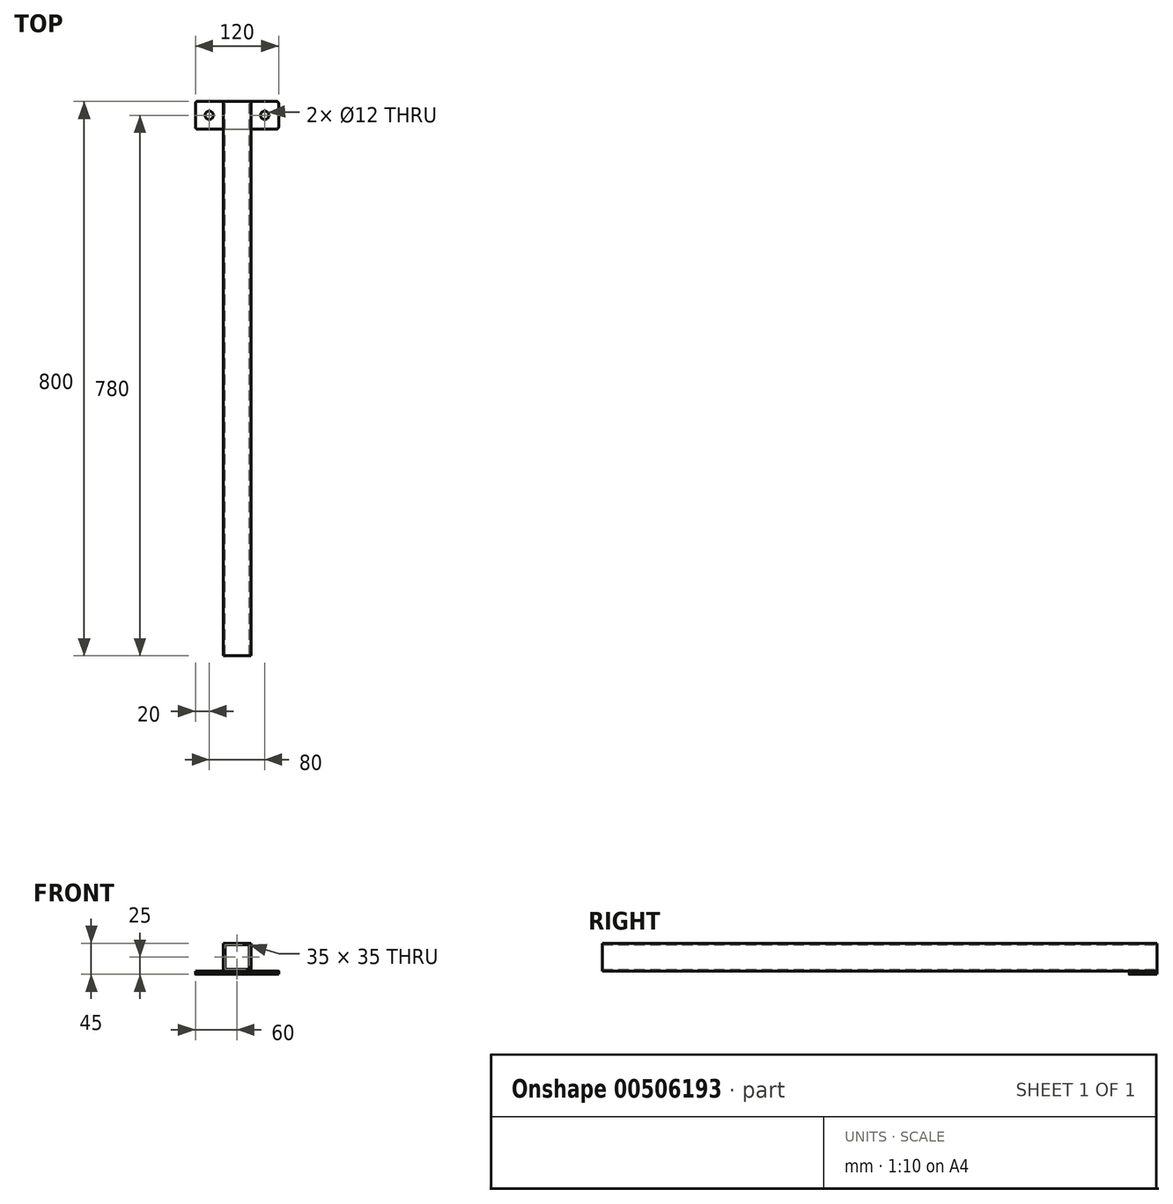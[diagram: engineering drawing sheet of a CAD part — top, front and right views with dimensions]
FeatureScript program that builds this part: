
annotation { "Feature Type Name" : "Feature", "Feature Type Description" : "" }
export const myFeature = defineFeature(function(context is Context, id is Id, definition is map)
    precondition{}
    {
        {
            var Q0;
            Q0=qCreatedBy(makeId("Front.planeOp"),FACE);
            var sketch = newSketch(context, id + "F0", { "sketchPlane" : qUnion([Q0])});
            skLineSegment(sketch, "E0.bottom", {"start": v(20, 20) * mm, "end": v(-20, 20) * mm});
            skLineSegment(sketch, "E0.top", {"start": v(20, -20) * mm, "end": v(-20, -20) * mm});
            skLineSegment(sketch, "E0.left", {"start": v(20, 20) * mm, "end": v(20, -20) * mm});
            skLineSegment(sketch, "E0.right", {"start": v(-20, 20) * mm, "end": v(-20, -20) * mm});
            skPoint(sketch, "E0.middle", {"position": v(0, 0) * mm});
            skLineSegment(sketch, "E1.bottom", {"start": v(17.5, 17.5) * mm, "end": v(-17.5, 17.5) * mm});
            skLineSegment(sketch, "E1.top", {"start": v(17.5, -17.5) * mm, "end": v(-17.5, -17.5) * mm});
            skLineSegment(sketch, "E1.left", {"start": v(17.5, 17.5) * mm, "end": v(17.5, -17.5) * mm});
            skLineSegment(sketch, "E1.right", {"start": v(-17.5, 17.5) * mm, "end": v(-17.5, -17.5) * mm});
            skSolve(sketch);
        }
        {
            var Q0;
            Q0 = qSketchRegion(id + "F0", true);
            extrude(context, id + "F1", {"entities" : qUnion([Q0]), "depth" : 800 * mm, "offsetDistance" : 25 * mm});
        }
        {
            var Q0;
            Q0=makeQuery(id+"F1.opExtrude","SWEPT_FACE",FACE,{"disambiguationData":[OSD([sQuery(id+"F0.wireOp",EDGE,"E0.top")])]});
            var sketch = newSketch(context, id + "F2", { "sketchPlane" : qUnion([Q0])});
            skLineSegment(sketch, "E2.bottom", {"start": v(-57, 0) * mm, "end": v(57, 0) * mm});
            skLineSegment(sketch, "E2.top", {"start": v(-57, 40) * mm, "end": v(57, 40) * mm});
            skLineSegment(sketch, "E2.left", {"start": v(-60, 3) * mm, "end": v(-60, 37) * mm});
            skLineSegment(sketch, "E2.right", {"start": v(60, 3) * mm, "end": v(60, 37) * mm});
            skCircle(sketch, "E3", {"center": v(-40, 20) * mm, "radius": 6 * mm});
            skPoint(sketch, "E3.centerSnap0", {"position": v(-60, 20) * mm});
            skCircle(sketch, "E4", {"center": v(40, 20) * mm, "radius": 6 * mm});
            skPoint(sketch, "E4.centerSnap0", {"position": v(60, 20) * mm});
            skPoint(sketch, "E5.visualSharp", {"position": v(-60, 40) * mm});
            skArc(sketch, "E5.filletArc", {"start": v(-57, 40) * mm, "mid": v(-59.12, 39.12) * mm, "end": v(-60, 37) * mm});
            skPoint(sketch, "E6.visualSharp", {"position": v(-60, 0) * mm});
            skArc(sketch, "E6.filletArc", {"start": v(-60, 3) * mm, "mid": v(-59.12, 0.88) * mm, "end": v(-57, 0) * mm});
            skPoint(sketch, "E7.visualSharp", {"position": v(60, 0) * mm});
            skArc(sketch, "E7.filletArc", {"start": v(57, 0) * mm, "mid": v(59.12, 0.88) * mm, "end": v(60, 3) * mm});
            skPoint(sketch, "E8.visualSharp", {"position": v(60, 40) * mm});
            skArc(sketch, "E8.filletArc", {"start": v(60, 37) * mm, "mid": v(59.12, 39.12) * mm, "end": v(57, 40) * mm});
            skSolve(sketch);
        }
        {
            var Q0;
            Q0 = qSketchRegion(id + "F2", true);
            extrude(context, id + "F3", {"entities" : qUnion([Q0]), "operationType" : NewBodyOperationType.ADD, "depth" : 5 * mm, "offsetDistance" : 25 * mm});
        }
    });
